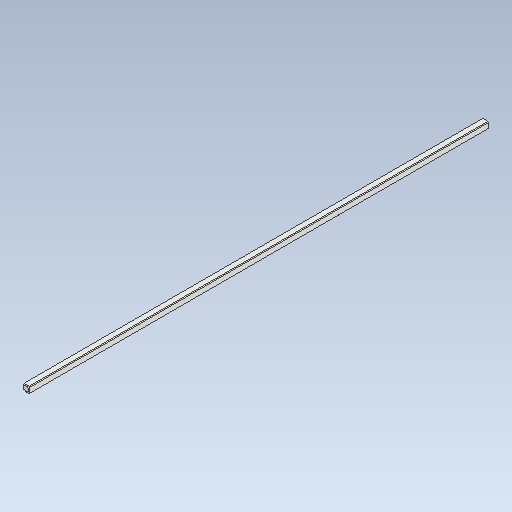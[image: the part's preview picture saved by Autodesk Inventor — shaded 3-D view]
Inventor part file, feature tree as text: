
AUTODESK INVENTOR PART (.ipt)
format: ipt  version: 2021 (Build 250183000, 183)  size: 102,912 bytes
history: mixed  units: in
note: dims shown in document units (in); Inventor stores cm internally (conversion verified against a paired STEP export)
features: mirror x1, imported_body x1
ambient origin geometry x8: Origin, YZ Plane, XZ Plane, XY Plane, X Axis, Y Axis, Z Axis, Center Point
bodies: Solid1 (imported_parasolid)
feature tree (2):
  mirror  "Mirror1"
  imported_body  NMx_Import_Brep_tag  [imported B-rep: ~12 faces, bbox_mm=[3.175, 3.175, 228.6]]
